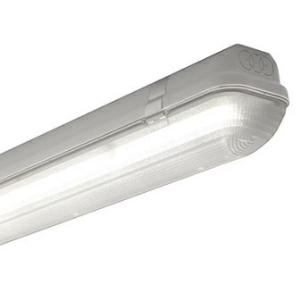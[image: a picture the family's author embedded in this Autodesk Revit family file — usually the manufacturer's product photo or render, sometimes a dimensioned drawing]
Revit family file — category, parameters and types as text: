
# Revit family: 3f_filippi_-_3f_linda_hq_3f_filippi_-_58869_-_3f_linda_led_1x24w-940_l1270
name_source: partatom
category: Lighting Fixtures
units: mm (PartAtom-declared; Revit-internal decimal feet)

## family parameters
Cut with Voids When Loaded = No
Host = Face
Light Source = No
Part Type = Normal
Room Calculation Point = No
Round Connector Dimension = Use Diameter
Shared = No

## types (1)
- 3F Filippi - 3F Linda HQ (1 x LED, 3150 lm, 28 W, 4000 K)
    Apparent Load = 28 VA
    Approval mark = CE
    CIE Flux Codes = 44 77 94 97 100
    Color Rendering = 90
    Color Temperature = 4000 K
    Control Gear = Electronic ballast
    Default Elevation = 1800 mm
    Description = ILLUMINOTECHNICAL
Luminous efficiency 100% (DLOR 97%, ULOR 3%).
Initial luminous flux of the luminaire 3150 lm.
Controlled symmetric distribution.
Installation Interdistance Transv.D = 1.77 x hu - Long.D = 1.17 x hu.
Tabular UGR (CIE 117 - 4H-8H; S=0.25H; 70/50/20): RUG 21.1 - 22.
Beam angle: 109° - 64°.
Luminous efficacy 113 lm/W.
Lifetime (L93/B10): 30000 h. (tq+25°C)
Lifetime (L90/B10): 50000 h. (tq+25°C)
Lifetime (L85/B10): 80000 h. (tq+25°C)
Lifetime (L80/B10): 100000 h. (tq+25°C)
Lifetime (L85/B10): 50000 h. (tq+35°C)
Sudden decreased luminous flux after 50000 hours: 0% (C0).
Photobiological safety in compliance with IEC/TR 62778: RG0 risk exempt, (IEC 62471).
In compliance with IEC/EN 62722-2-1 - IEC/EN 62717 standards.

SOURCE
Linear LED module 24W/940.
Energy efficiency class (UE 2019/2020 - UE 2019/2015): E.
CIE 13.3 Colour rendering index: CRI >90 (R9 >50%).
IES TM-30 Fidelity Index: Rf = 92 Rg = 101.
CCT nominal colour temperature 4000 K.
Colour initial tolerance (MacAdam): SDCM 3.

MECHANICAL
Self-extinguishing V2 polycarbonate housing, injection moulded, RAL 7035 grey.
Ecologic anti-aging injected sealing gasket.
Diffuser in self-extinguishing V2 polycarbonate, photo-engraved interior, UV stabilised, injection moulded with smooth outer surface, tamper-proof opening.
Gear-holder reflector in hot-dip galvanised steel, painted with white polyester base.
Snug fit safety snap-lock clips for diffuser mounting in stainless steel, screwdriver opening.
Fixing brackets in stainless steel.
Possibility for technicians to access the interior of the luminaire.
Luminaire with limited surface temperature. - D - (EN 60598-2-24)
Dimensions: 1270x100 mm, height 100 mm. Weight 2.089 kg.
IP66 protection degree.
Mechanical strength to impacts IK10 (20 joule).
Glow-wire test resistance 850°C.

ELECTRICAL
Halogen Free electronic wiring 230V-50/60Hz, power factor 0.90, THD <25%, constant output current, SELV, class I, 1 driver.
Power of the luminaire 28 W.
ENEC - CE.
SAFE FLICKER: PstLM=<1 and SVM=<0.4 (IEC TR 61547-1 and IEC TR 63158), to ensure a more comfortable and safe light.
Luminaire compliant with EN 60598-2-22 for power supply from a centralised emergency system CPSS (Central Power Supply System), not incorporated in the luminaire - high risk areas excluded. The default power and flux are 100% in AC and 100% in DC.
Ambient temperature from -20°C to +35°C.
Temperature class T6 max 85°C.
Relative humidity UR: <85%.

INSTALLATION
Ceiling / Suspended / Wall.
All accessories dedicated to this product are available on the Catalog and on our website www.3F-Filippi.com.

APPLICATIONS
Suitable product for food production plants (HACCP), IFS (Food Version 6), BRC (GSFS Food Version 7).
Dry, dusty indoor environments, subject to occasional water splashes.
Virtually shatterproof polycarbonate compatibly with the fumes / atmospheres that compromise the elasticity of plastic materials.
Not suitable for installation on surfaces subject to important vibrations, exposed to weather conditions, on ropes or poles.
Suitable for illumination of public car parks and parking grounds referred to DIN 67528:2018-04.

WARNING
Fixture not suitable for cold stores with an ambient temperature <0°C and/or relative humidity >85%.
Luminaire designed for disposal/recycling at end-of-life.
Replaceable (LED only) light source by a professional. Replaceable control gear by a professional.
    Height = 100 mm  [stored 0.328084 ft]
    Lamp = 1 x LED
    Lamp Light Flux = 3150 lm
    Lamp Power = 28 W
    Lamp count = 1
    Length = 1270 mm
    Lifetime = 50000 h
    Luminous efficacy = 113 lm/W
    Manufacturer = 3F Filippi
    ModVariant = No
    Model = 3F Filippi - 58869 - 3F Linda LED 1x24W-940 L1270
    Mounting Place = Ceiling
    Mounting Type = Pendant
    Number of Poles = 1
    OnlyDefault = Yes
    Power Factor = 1
    Product Name = 3F Filippi - 3F Linda HQ
    Product group = pendant luminaire
    ProductGroupID = 9
    Protection Class = Protection class I
    Protection Degree = IP 66
    RLX_Detail_Level = 1
    RLX_Emergency_Light_Flux = 0 lm
    RLX_Emergency_Type = 0
    RLX_Emergency_Type_DB = No
    RlxData = <blob elided: 68633 chars, md5=a6d761f2>
    Socket = socket
    Standby Power = 0 W
    System Light Flux = 3150 lm
    System Power = 28 W
    Type Comments = Product without accessories
    Type Image = 3ffilippi_3f_linda_led_1x.jpg
    URL = http://relux.com
    VarID = ---
    Voltage = 0 V
    Weight = 0.00 kg
    Width = 100 mm  [stored 0.328084 ft]

note: [stored X ft] marks values corroborated as IEEE doubles in the binary element streams (Revit-internal decimal feet)

## geometry (parser evidence)
native form markers: Blend x4, Sweep x9
no freeform markers — native parametric forms only
